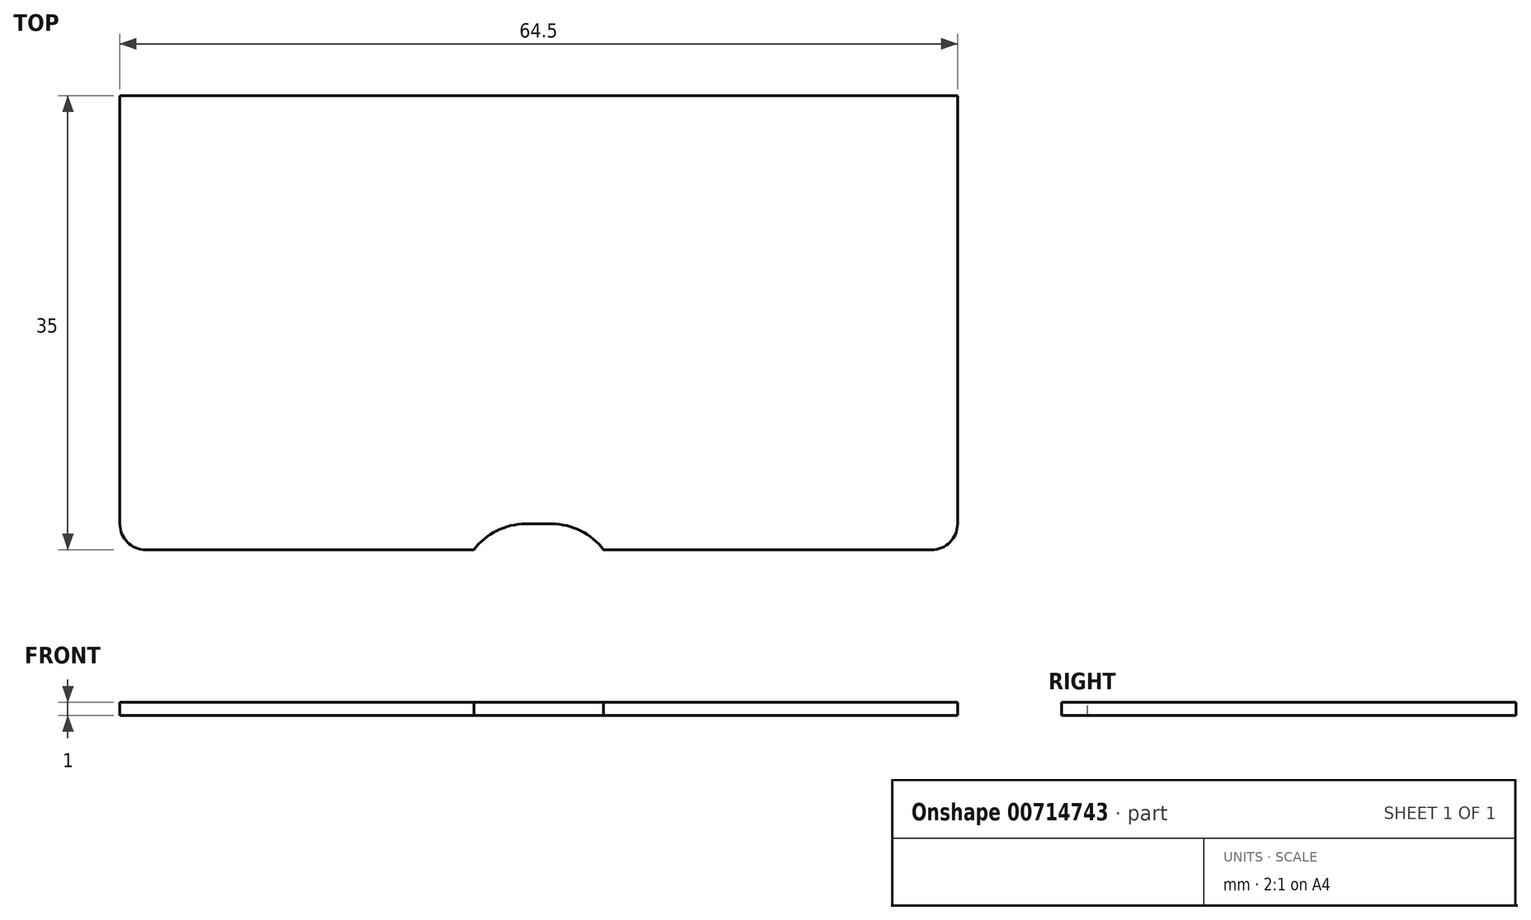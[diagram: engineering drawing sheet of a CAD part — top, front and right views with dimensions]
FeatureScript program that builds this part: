
annotation { "Feature Type Name" : "Feature", "Feature Type Description" : "" }
export const myFeature = defineFeature(function(context is Context, id is Id, definition is map)
    precondition{}
    {
        {
            var Q0;
            Q0=qCreatedBy(makeId("Top.planeOp"),FACE);
            var sketch = newSketch(context, id + "F0", { "sketchPlane" : qUnion([Q0])});
            skLineSegment(sketch, "E0.bottom", {"start": v(-32.25, 16.73) * mm, "end": v(32.25, 16.73) * mm});
            skLineSegment(sketch, "E0.top", {"start": v(-32.25, -18.27) * mm, "end": v(32.25, -18.27) * mm});
            skLineSegment(sketch, "E0.left", {"start": v(-32.25, 16.73) * mm, "end": v(-32.25, -18.27) * mm});
            skLineSegment(sketch, "E0.right", {"start": v(32.25, 16.73) * mm, "end": v(32.25, -18.27) * mm});
            skPoint(sketch, "E1.snap10", {"position": v(0, -18.27) * mm});
            skSolve(sketch);
        }
        {
            var Q0;
            Q0 = qSketchRegion(id + "F0", true);
            extrude(context, id + "F1", {"entities" : qUnion([Q0]), "depth" : 1 * mm, "offsetDistance" : 25 * mm});
        }
        {
            var Q0;
            Q0=makeQuery(id+"F1.opExtrude","SWEPT_EDGE",EDGE,{"disambiguationData":[OSD([sQuery(id+"F0.wireOp",EDGE,"E0.top"),sQuery(id+"F0.wireOp",EDGE,"E0.left")])]});
            var Q1;
            Q1=makeQuery(id+"F1.opExtrude","SWEPT_EDGE",EDGE,{"disambiguationData":[OSD([sQuery(id+"F0.wireOp",EDGE,"E0.top"),sQuery(id+"F0.wireOp",EDGE,"E0.right")])]});
            fillet(context, id + "F2", {"entities" : qUnion([Q0, Q1]), "radius" : 2 * mm, "tangentPropagation" : true, "allowEdgeOverflow" : false});
        }
        {
            var Q0;
            Q0=makeQuery(id+"F1.opExtrude","SWEPT_FACE",FACE,{"disambiguationData":[OSD([sQuery(id+"F0.wireOp",EDGE,"E0.top")])]});
            var sketch = newSketch(context, id + "F3", { "sketchPlane" : qUnion([Q0])});
            skLineSegment(sketch, "E2.bottom", {"start": v(-5, 1) * mm, "end": v(5, 1) * mm});
            skLineSegment(sketch, "E2.top", {"start": v(-5, 0) * mm, "end": v(5, 0) * mm});
            skLineSegment(sketch, "E2.left", {"start": v(-5, 1) * mm, "end": v(-5, 0) * mm});
            skLineSegment(sketch, "E2.right", {"start": v(5, 1) * mm, "end": v(5, 0) * mm});
            skSolve(sketch);
        }
        {
            var Q0;
            Q0 = qSketchRegion(id + "F3", true);
            extrude(context, id + "F4", {"entities" : qUnion([Q0]), "operationType" : NewBodyOperationType.REMOVE, "oppositeDirection" : true, "depth" : 2 * mm, "offsetDistance" : 25 * mm});
        }
        {
            var Q0;
            Q0=makeQuery(id+"F4.boolean.opBoolean","COPY",EDGE,{"derivedFrom":makeQuery(id+"F4.opExtrude","CAP_EDGE",EDGE,{"disambiguationData":[OSD([sQuery(id+"F3.wireOp",EDGE,"E2.right")])],"isStart":false})});
            var Q1;
            Q1=makeQuery(id+"F4.boolean.opBoolean","COPY",EDGE,{"derivedFrom":makeQuery(id+"F4.opExtrude","CAP_EDGE",EDGE,{"disambiguationData":[OSD([sQuery(id+"F3.wireOp",EDGE,"E2.left")])],"isStart":false})});
            fillet(context, id + "F5", {"entities" : qUnion([Q0, Q1]), "radius" : 5 * mm, "tangentPropagation" : true, "allowEdgeOverflow" : false});
        }
    });
